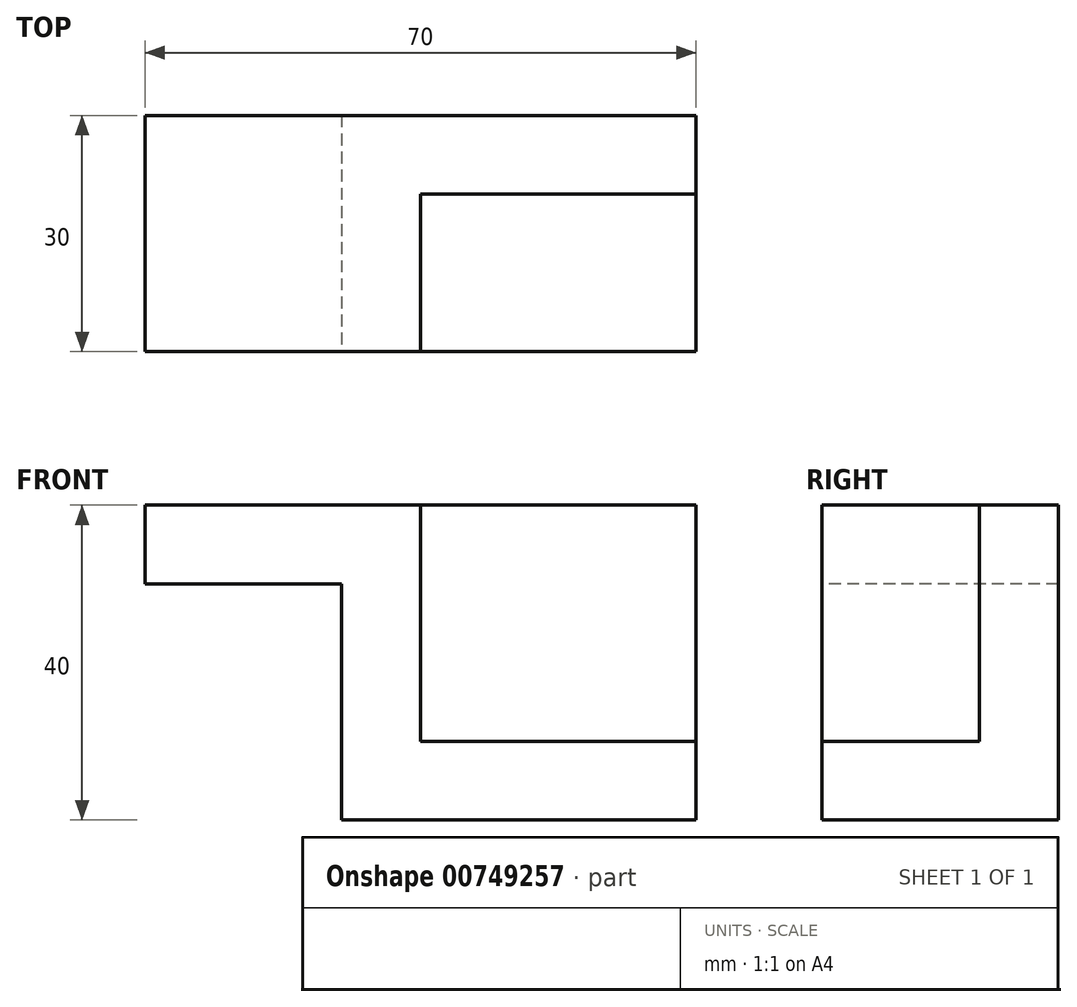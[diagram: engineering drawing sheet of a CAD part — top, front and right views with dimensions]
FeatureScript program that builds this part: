
annotation { "Feature Type Name" : "Feature", "Feature Type Description" : "" }
export const myFeature = defineFeature(function(context is Context, id is Id, definition is map)
    precondition{}
    {
        {
            var Q0;
            Q0=qCreatedBy(makeId("Front.planeOp"),FACE);
            var sketch = newSketch(context, id + "F0", { "sketchPlane" : qUnion([Q0])});
            skLineSegment(sketch, "E0.bottom", {"start": v(-35, -20) * mm, "end": v(35, -20) * mm});
            skLineSegment(sketch, "E0.top", {"start": v(-35, 20) * mm, "end": v(35, 20) * mm});
            skLineSegment(sketch, "E0.left", {"start": v(-35, -20) * mm, "end": v(-35, 20) * mm});
            skLineSegment(sketch, "E0.right", {"start": v(35, -20) * mm, "end": v(35, 20) * mm});
            skPoint(sketch, "E0.middle", {"position": v(0, 0) * mm});
            skSolve(sketch);
        }
        {
            var Q0;
            Q0=makeQuery(id+"F0.imprint","IMPRINT",FACE,{"disambiguationData":[TD([[makeQuery(id+"F0.imprint","IMPRINT",EDGE,{"derivedFrom":sQuery(id+"F0.wireOp",EDGE,"E0.bottom")}),1.0]])]});
            extrude(context, id + "F1", {"entities" : qUnion([Q0]), "depth" : 30 * mm, "offsetDistance" : 25 * mm});
        }
        {
            var Q0;
            Q0=makeQuery(id+"F1.opExtrude","CAP_FACE",FACE,{"disambiguationData":[OSD([sQuery(id+"F0.wireOp",EDGE,"E0.bottom"),sQuery(id+"F0.wireOp",EDGE,"E0.top"),sQuery(id+"F0.wireOp",EDGE,"E0.left"),sQuery(id+"F0.wireOp",EDGE,"E0.right")])],"isStart":false});
            var sketch = newSketch(context, id + "F2", { "sketchPlane" : qUnion([Q0])});
            skLineSegment(sketch, "E1.left", {"start": v(0, 0) * mm, "end": v(0, 0) * mm});
            skLineSegment(sketch, "E1.right", {"start": v(35, 0) * mm, "end": v(35, 0) * mm});
            skLineSegment(sketch, "E2.bottom", {"start": v(35, 20) * mm, "end": v(0, 20) * mm});
            skLineSegment(sketch, "E2.left", {"start": v(35, 20) * mm, "end": v(35, 0) * mm});
            skLineSegment(sketch, "E2.right", {"start": v(0, 20) * mm, "end": v(0, 0) * mm});
            skLineSegment(sketch, "E3", {"start": v(0, 4.1) * mm, "end": v(0, -10) * mm});
            skLineSegment(sketch, "E4", {"start": v(0, -10) * mm, "end": v(35, -10) * mm});
            skLineSegment(sketch, "E5", {"start": v(35, -10) * mm, "end": v(35, 0) * mm});
            skSolve(sketch);
        }
        {
            var Q0;
            Q0=makeQuery(id+"F2.imprint","IMPRINT",FACE,{"disambiguationData":[TD([[makeQuery(id+"F2.imprint","IMPRINT",EDGE,{"derivedFrom":sQuery(id+"F2.wireOp",EDGE,"E2.bottom")}),-1.0]])]});
            extrude(context, id + "F3", {"entities" : qUnion([Q0]), "operationType" : NewBodyOperationType.REMOVE, "oppositeDirection" : true, "depth" : 20 * mm, "offsetDistance" : 25 * mm});
        }
        {
            var Q0;
            Q0=makeQuery(id+"F1.opExtrude","CAP_FACE",FACE,{"disambiguationData":[OSD([sQuery(id+"F0.wireOp",EDGE,"E0.bottom"),sQuery(id+"F0.wireOp",EDGE,"E0.top"),sQuery(id+"F0.wireOp",EDGE,"E0.left"),sQuery(id+"F0.wireOp",EDGE,"E0.right")])],"isStart":false});
            var sketch = newSketch(context, id + "F4", { "sketchPlane" : qUnion([Q0])});
            skLineSegment(sketch, "E6.bottom", {"start": v(-35, 10) * mm, "end": v(-10, 10) * mm});
            skLineSegment(sketch, "E6.top", {"start": v(-35, -20) * mm, "end": v(-10, -20) * mm});
            skLineSegment(sketch, "E6.left", {"start": v(-35, 10) * mm, "end": v(-35, -20) * mm});
            skLineSegment(sketch, "E6.right", {"start": v(-10, 10) * mm, "end": v(-10, -20) * mm});
            skSolve(sketch);
        }
        {
            var Q0;
            Q0=makeQuery(id+"F4.imprint","IMPRINT",FACE,{"disambiguationData":[TD([[makeQuery(id+"F4.imprint","IMPRINT",EDGE,{"derivedFrom":sQuery(id+"F4.wireOp",EDGE,"E6.bottom")}),-1.0]])]});
            extrude(context, id + "F5", {"entities" : qUnion([Q0]), "operationType" : NewBodyOperationType.REMOVE, "endBound" : BoundingType.THROUGH_ALL, "oppositeDirection" : true, "depth" : 25 * mm, "offsetDistance" : 25 * mm});
        }
    });
